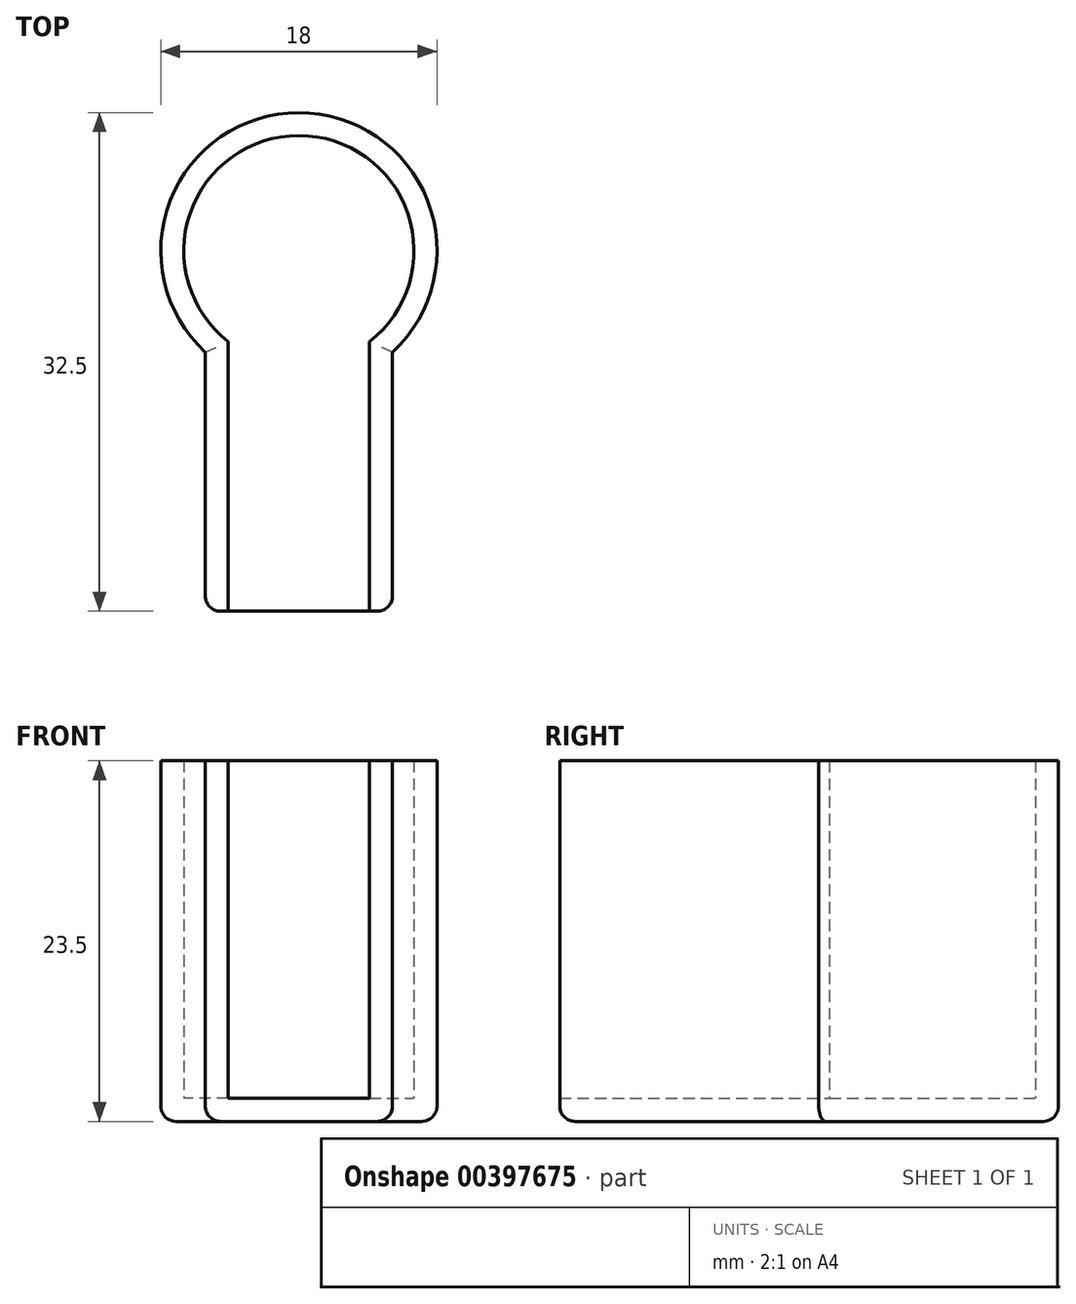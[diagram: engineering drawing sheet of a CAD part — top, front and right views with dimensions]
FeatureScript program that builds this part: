
annotation { "Feature Type Name" : "Feature", "Feature Type Description" : "" }
export const myFeature = defineFeature(function(context is Context, id is Id, definition is map)
    precondition{}
    {
        {
            var Q0;
            Q0=qCreatedBy(makeId("Top.planeOp"),FACE);
            var sketch = newSketch(context, id + "F0", { "sketchPlane" : qUnion([Q0])});
            skLineSegment(sketch, "E0.bottom", {"start": v(-4.6, -22) * mm, "end": v(4.6, -22) * mm});
            skLineSegment(sketch, "E0.left", {"start": v(-4.6, -22) * mm, "end": v(-4.6, -5.92) * mm});
            skLineSegment(sketch, "E0.right", {"start": v(4.6, -22) * mm, "end": v(4.6, -5.92) * mm});
            skArc(sketch, "E1", {"start": v(4.6, -5.92) * mm, "mid": v(0, 7.5) * mm, "end": v(-4.6, -5.92) * mm});
            skSolve(sketch);
        }
        {
            var Q0;
            Q0 = qSketchRegion(id + "F0", true);
            extrude(context, id + "F1", {"entities" : qUnion([Q0]), "depth" : 22 * mm});
        }
        {
            var Q0;
            Q0=makeQuery(id+"F1.opExtrude","CAP_FACE",FACE,{"disambiguationData":[OSD([sQuery(id+"F0.wireOp",EDGE,"E0.bottom"),sQuery(id+"F0.wireOp",EDGE,"E0.left"),sQuery(id+"F0.wireOp",EDGE,"E0.right"),sQuery(id+"F0.wireOp",EDGE,"E1")])],"isStart":false});
            shell(context, id + "F2", {"entities" : qUnion([Q0]), "thickness" : 1.5 * mm, "oppositeDirection" : true});
        }
        {
            var Q0;
            Q0=makeQuery(id+"F1.opExtrude","SWEPT_FACE",FACE,{"disambiguationData":[OSD([sQuery(id+"F0.wireOp",EDGE,"E0.bottom")])]});
            var sketch = newSketch(context, id + "F3", { "sketchPlane" : qUnion([Q0])});
            skLineSegment(sketch, "E2.bottom", {"start": v(-4.6, 22) * mm, "end": v(4.6, 22) * mm});
            skLineSegment(sketch, "E2.top", {"start": v(-4.6, 0) * mm, "end": v(4.6, 0) * mm});
            skLineSegment(sketch, "E2.left", {"start": v(-4.6, 22) * mm, "end": v(-4.6, 0) * mm});
            skLineSegment(sketch, "E2.right", {"start": v(4.6, 22) * mm, "end": v(4.6, 0) * mm});
            skSolve(sketch);
        }
        {
            var Q0;
            Q0 = qSketchRegion(id + "F3", true);
            extrude(context, id + "F4", {"entities" : qUnion([Q0]), "operationType" : NewBodyOperationType.REMOVE, "endBound" : BoundingType.UP_TO_NEXT, "oppositeDirection" : true, "depth" : 25 * mm});
        }
        {
            var Q0;
            Q0=makeQuery(id+"F1.opExtrude","CAP_EDGE",EDGE,{"disambiguationData":[OSD([sQuery(id+"F0.wireOp",EDGE,"E1")])],"isStart":true});
            var Q1;
            Q1=makeQuery(id+"F1.opExtrude","CAP_EDGE",EDGE,{"disambiguationData":[OSD([sQuery(id+"F0.wireOp",EDGE,"E0.right")])],"isStart":true});
            var Q2;
            Q2=makeQuery(id+"F1.opExtrude","CAP_EDGE",EDGE,{"disambiguationData":[OSD([sQuery(id+"F0.wireOp",EDGE,"E0.left")])],"isStart":true});
            var Q3;
            Q3=makeQuery(id+"F1.opExtrude","CAP_EDGE",EDGE,{"disambiguationData":[OSD([sQuery(id+"F0.wireOp",EDGE,"E0.bottom")])],"isStart":true});
            var Q4;
            Q4=makeQuery(id+"F1.opExtrude","SWEPT_EDGE",EDGE,{"disambiguationData":[OSD([sQuery(id+"F0.wireOp",EDGE,"E0.bottom"),sQuery(id+"F0.wireOp",EDGE,"E0.right")])]});
            var Q5;
            Q5=makeQuery(id+"F1.opExtrude","SWEPT_EDGE",EDGE,{"disambiguationData":[OSD([sQuery(id+"F0.wireOp",EDGE,"E0.bottom"),sQuery(id+"F0.wireOp",EDGE,"E0.left")])]});
            fillet(context, id + "F5", {"entities" : qUnion([Q0, Q1, Q2, Q3, Q4, Q5]), "radius" : 1 * mm, "tangentPropagation" : true, "allowEdgeOverflow" : false});
        }
    });
